# Revit family: NBS_HeatraeSadia_DrnkngFntnPckgs_Superchill_25F
name_source: partatom
category: Plumbing Fixtures
revit_build: Autodesk Revit 2014 (Build: 20130709_2115(x64)
units: mm (PartAtom-declared; Revit-internal decimal feet)

## types (1)
- Superchill25F
    AssetType = Fixed
    BIMObjectName = NBS_HeatraeSadia_DrinkingFountainPackages_Superchill25F
    BodyHeight = 960 mm  [stored 3.14961 ft]
    CW Connection = Yes
    Color = Natural
    CompressorPower = 1/6 hp
    Connections = 8 mm female push fit inlet connection with supplied 8 mm male adapter, 24 mm drain tube
    Controls = Lever-operated filler tap and push button
    Depth = 340 mm  [stored 1.11549 ft]
    Description = Chilled drinking water fountain
    DurationUnit = year
    ElectricalDeviceNominalPower = 0
    Features = For use in offices, factories and other public buildings, supplied with both a filler tap and water fountain, factory-fitted with in-line water filter for added water purity, fan-cooled condenser
    Finish = Brushed
    FlowRate = 25 L/hr
    FormUnit = Floor mounted
    FormWastes = Integral 1¼" BSP waste outlet connection
    FormWaterSupply = Chilled, filtered supply to jet
    HW Connection = No
    HasProtectiveEarth = No
    Height = 1230 mm  [stored 4.03543 ft]
    IPCode = IPX2
    IfcExportAs = IfcElectricApplianceType
    IfcExportType = FREESTANDINGWATERCOOLER
    In-lineFilterSystem = Factory-fitted Everpure QL3 head with replaceable cartridge (Everpure 4C), 0.5 micron filtration, taste and odour eliminating
    IntegralAccessories = Cup holder (95:970:127)
    ManufacturerName = Heatrae Sadia
    ManufacturerURL = www.heatraesadia.com
    Material = Outer casing: Stainless steel effect plastic-coated, corrosion proofed steel; Water collection sink: Stainless steel
    ModelNumber = 95:200:225
    ModelReference = Superchill 25F
    NBSCertification = http://www.nationalbimlibrary.com
    NBSDescription = Drinking fountain packages
    NBSReference = 45-35-70/400
    Name = DrinkingFountainPackages_Superchill25F_HeatraeSadia
    NominalCurrent = 0
    NominalFrequencyRange = 0
    NominalHeight = 1230 mm  [stored 4.03543 ft]
    NominalLength = 340 mm  [stored 1.11549 ft]
    NominalVoltage = 230.0, 240.0
    NominalWidth = 325 mm  [stored 1.06627 ft]
    NumberOfPoles = 0
    OutletTemperatureRange = 6-12°C
    PhaseAngle = 0.00°
    ProductInformation = www.heatraesadia.com/docs/Drinking_water_brochure.pdf
    Size = 1230 x 325 x 340 mm
    StorageWaterHeaterMaterial = NBS_Concept
    SupplyPressureRange = 1.0-3.5 bar
    ThirdPartyCertification = WRAS listed
    Uniclass2 = 45-90-46/428
    Uniclass2015Description = Drinking fountains
    Uniclass2015Reference = Pr_40_20_87_24
    Uniclass2015Version = Products v1.1
    UsageCurrent = 0
    Vent Connection = No
    Version = 1
    WarrantyDurationLabor = 2
    WarrantyDurationParts = 2
    WarrantyDurationUnit = year
    WarrantyStartDate = 1900-12-31T23:59:59
    Waste Connection = Yes
    WaterChillingSystem = 5 L capacity, grade 304 (1.4301) stainless steel chilling tank
    Weight = 34 kg (full)
    Width = 325 mm  [stored 1.06627 ft]

note: [stored X ft] marks values corroborated as IEEE doubles in the binary element streams (Revit-internal decimal feet)

## geometry (parser evidence)
native form markers: Sweep x3
no freeform markers — native parametric forms only
